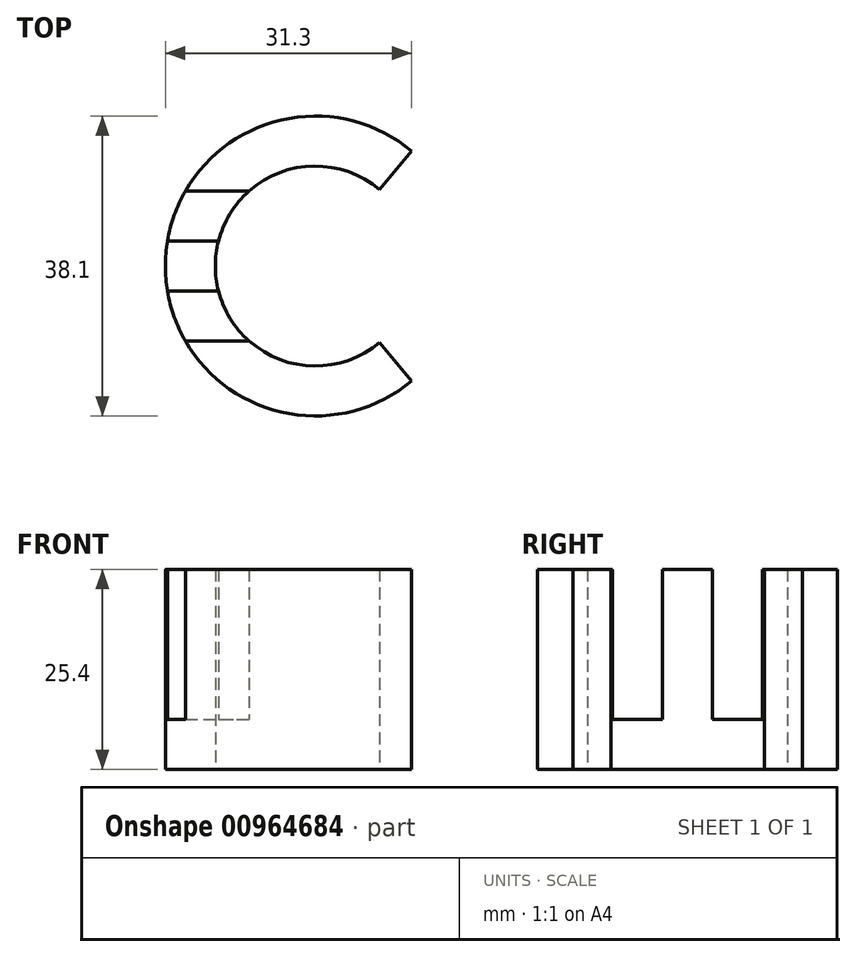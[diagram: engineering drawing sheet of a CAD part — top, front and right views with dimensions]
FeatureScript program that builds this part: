
annotation { "Feature Type Name" : "Feature", "Feature Type Description" : "" }
export const myFeature = defineFeature(function(context is Context, id is Id, definition is map)
    precondition{}
    {
        {
            var Q0;
            Q0=qCreatedBy(makeId("Top.planeOp"),FACE);
            var sketch = newSketch(context, id + "F0", { "sketchPlane" : qUnion([Q0])});
            skArc(sketch, "E0", {"start": v(12.25, 14.6) * mm, "mid": v(-19.05, 0) * mm, "end": v(12.25, -14.6) * mm});
            skArc(sketch, "E1", {"start": v(8.16, 9.73) * mm, "mid": v(-12.7, 0) * mm, "end": v(8.16, -9.73) * mm});
            skLineSegment(sketch, "E2", {"start": v(8.16, 9.73) * mm, "end": v(12.25, 14.6) * mm});
            skLineSegment(sketch, "E3", {"start": v(8.16, -9.73) * mm, "end": v(12.25, -14.6) * mm});
            skSolve(sketch);
        }
        {
            var Q0;
            Q0=makeQuery(id+"F0.imprint","IMPRINT",FACE,{"disambiguationData":[TD([[makeQuery(id+"F0.imprint","IMPRINT",EDGE,{"derivedFrom":sQuery(id+"F0.wireOp",EDGE,"E0")}),1.0]])]});
            extrude(context, id + "F1", {"entities" : qUnion([Q0]), "depth" : 25.4 * mm, "offsetDistance" : 25.4 * mm});
        }
        {
            var Q0;
            Q0=qCreatedBy(makeId("Right.planeOp"),FACE);
            var sketch = newSketch(context, id + "F2", { "sketchPlane" : qUnion([Q0])});
            skLineSegment(sketch, "E4.bottom", {"start": v(9.53, 6.35) * mm, "end": v(3.18, 6.35) * mm});
            skLineSegment(sketch, "E4.top", {"start": v(9.52, 25.4) * mm, "end": v(3.17, 25.4) * mm});
            skLineSegment(sketch, "E4.left", {"start": v(9.53, 6.35) * mm, "end": v(9.52, 25.4) * mm});
            skLineSegment(sketch, "E4.right", {"start": v(3.18, 6.35) * mm, "end": v(3.17, 25.4) * mm});
            skLineSegment(sketch, "E5.bottom", {"start": v(-3.18, 25.4) * mm, "end": v(-9.53, 25.4) * mm});
            skLineSegment(sketch, "E5.top", {"start": v(-3.17, 6.35) * mm, "end": v(-9.52, 6.35) * mm});
            skLineSegment(sketch, "E5.left", {"start": v(-3.18, 25.4) * mm, "end": v(-3.17, 6.35) * mm});
            skLineSegment(sketch, "E5.right", {"start": v(-9.53, 25.4) * mm, "end": v(-9.52, 6.35) * mm});
            skSolve(sketch);
        }
        {
            var Q0;
            Q0 = qSketchRegion(id + "F2", true);
            extrude(context, id + "F3", {"entities" : qUnion([Q0]), "operationType" : NewBodyOperationType.REMOVE, "oppositeDirection" : true, "depth" : 25.4 * mm, "offsetDistance" : 25.4 * mm});
        }
    });
